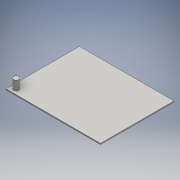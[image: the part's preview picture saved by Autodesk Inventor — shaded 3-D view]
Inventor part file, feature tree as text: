
AUTODESK INVENTOR PART (.ipt)
format: ipt  version: 2016 (Build 200138000, 138)  size: 91,648 bytes
history: native  units: mm
features: extrude x2, sketch x1
ambient origin geometry x8: Origin, YZ Plane, XZ Plane, XY Plane, X Axis, Y Axis, Z Axis, Center Point
bodies: Solid1 (feature_tree)
feature tree (3):
  sketch  "Sketch1"  dims[d0=90.0mm d1=70.0mm d6=1.0mm d7=0.0mm d8=10.0mm d9=0.0mm]
  extrude  "Extrusion1"  Depth=70.0mm
  extrude  "Extrusion2"  Depth=1.0mm TaperAngle=0.0deg
